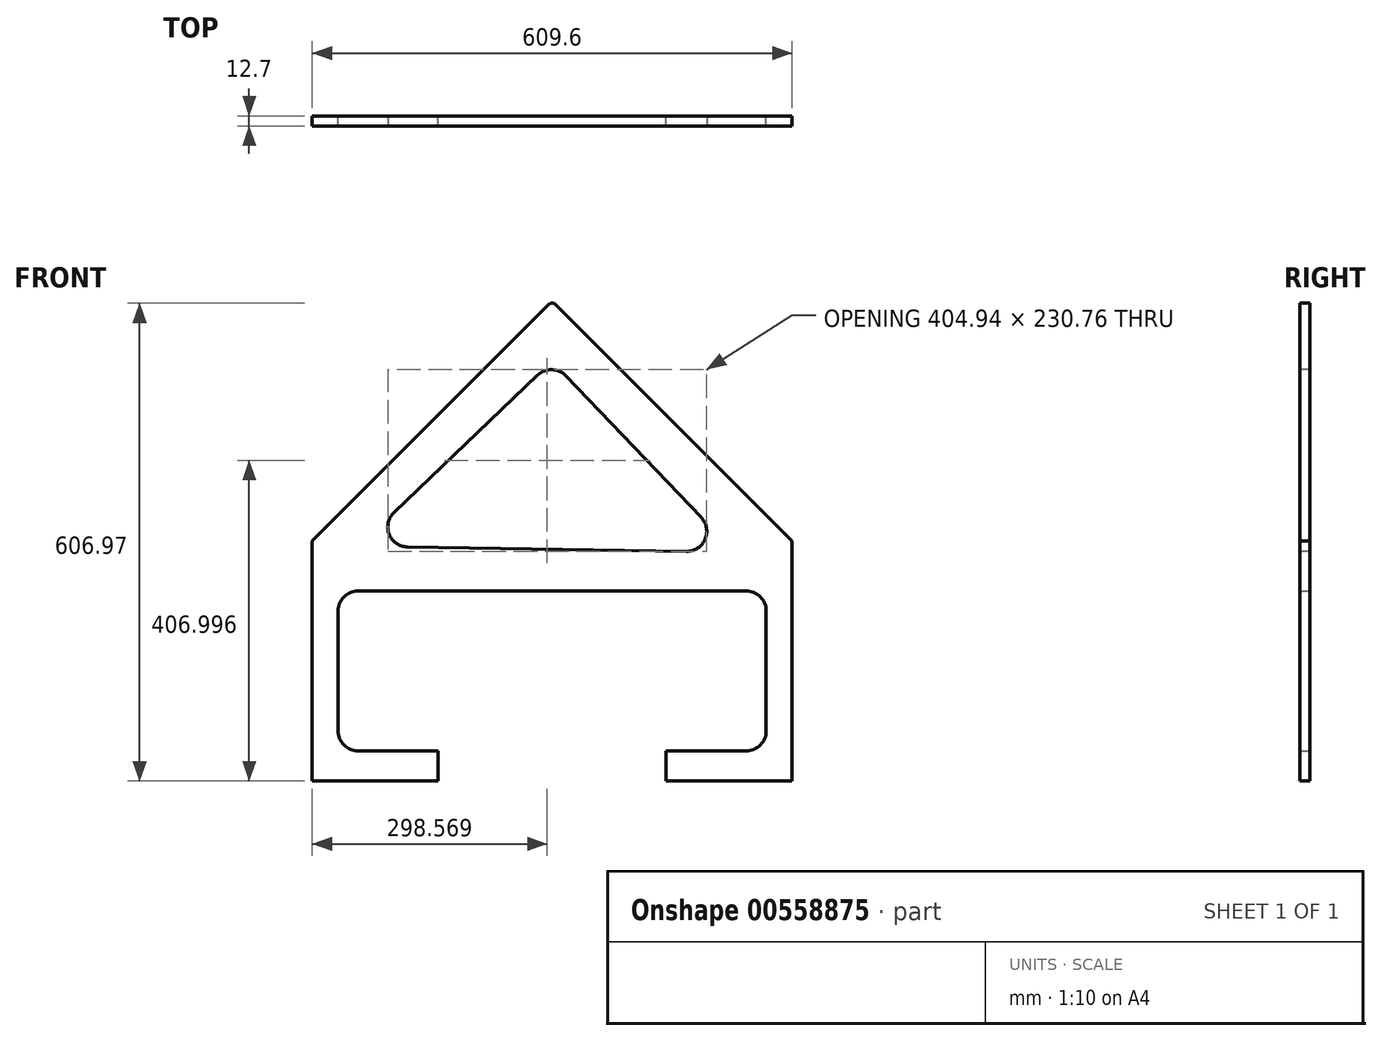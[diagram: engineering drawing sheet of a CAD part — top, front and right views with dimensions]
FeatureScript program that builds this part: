
annotation { "Feature Type Name" : "Feature", "Feature Type Description" : "" }
export const myFeature = defineFeature(function(context is Context, id is Id, definition is map)
    precondition{}
    {
        {
            var Q0;
            Q0=qCreatedBy(makeId("Front.planeOp"),FACE);
            var sketch = newSketch(context, id + "F0", { "sketchPlane" : qUnion([Q0])});
            skLineSegment(sketch, "E0", {"start": v(-304.8, 0) * mm, "end": v(-304.8, 304.8) * mm});
            skLineSegment(sketch, "E1", {"start": v(-304.8, 304.8) * mm, "end": v(0, 609.6) * mm});
            skLineSegment(sketch, "E2", {"start": v(-304.8, 0) * mm, "end": v(-144.82, 0) * mm});
            skLineSegment(sketch, "E3", {"start": v(-144.82, 0) * mm, "end": v(-144.82, 38.1) * mm});
            skLineSegment(sketch, "E4", {"start": v(-144.82, 38.1) * mm, "end": v(-271.82, 38.1) * mm});
            skLineSegment(sketch, "E5", {"start": v(-271.82, 38.1) * mm, "end": v(-271.82, 241.3) * mm});
            skLineSegment(sketch, "E6", {"start": v(-271.82, 241.3) * mm, "end": v(0, 241.3) * mm});
            skLineSegment(sketch, "E7", {"start": v(0, 287.8) * mm, "end": v(-247.66, 287.8) * mm, "construction": true});
            skLineSegment(sketch, "E8", {"start": v(-247.66, 287.8) * mm, "end": v(0, 535.45) * mm, "construction": true});
            skLineSegment(sketch, "E9.MirrorCS", {"start": v(304.8, 304.8) * mm, "end": v(0, 609.6) * mm});
            skLineSegment(sketch, "E10.MirrorCS", {"start": v(247.66, 287.8) * mm, "end": v(0, 535.45) * mm, "construction": true});
            skLineSegment(sketch, "E11.MirrorCS", {"start": v(0, 287.8) * mm, "end": v(247.66, 287.8) * mm, "construction": true});
            skLineSegment(sketch, "E12.MirrorCS", {"start": v(271.82, 241.3) * mm, "end": v(0, 241.3) * mm});
            skLineSegment(sketch, "E13.MirrorCS", {"start": v(304.8, 0) * mm, "end": v(304.8, 304.8) * mm});
            skLineSegment(sketch, "E14.MirrorCS", {"start": v(271.82, 38.1) * mm, "end": v(271.82, 241.3) * mm});
            skLineSegment(sketch, "E15.MirrorCS", {"start": v(144.82, 38.1) * mm, "end": v(271.82, 38.1) * mm});
            skLineSegment(sketch, "E16.MirrorCS", {"start": v(304.8, 0) * mm, "end": v(144.82, 0) * mm});
            skLineSegment(sketch, "E17.MirrorCS", {"start": v(144.82, 0) * mm, "end": v(144.82, 38.1) * mm});
            skSolve(sketch);
        }
        {
            var Q0;
            Q0=makeQuery(id+"F0.imprint","IMPRINT",FACE,{"disambiguationData":[TD([[makeQuery(id+"F0.imprint","IMPRINT",EDGE,{"derivedFrom":sQuery(id+"F0.wireOp",EDGE,"E0")}),-1.0]])]});
            extrude(context, id + "F1", {"entities" : qUnion([Q0]), "depth" : 12.7 * mm, "offsetDistance" : 25.4 * mm});
        }
        {
            var Q0;
            Q0=qCreatedBy(makeId("Front.planeOp"),FACE);
            var sketch = newSketch(context, id + "F2", { "sketchPlane" : qUnion([Q0])});
            skLineSegment(sketch, "E18", {"start": v(-245.72, 298.27) * mm, "end": v(0, 532.9) * mm});
            skLineSegment(sketch, "E19", {"start": v(0, 532.9) * mm, "end": v(231.31, 290.65) * mm});
            skLineSegment(sketch, "E20", {"start": v(231.31, 290.65) * mm, "end": v(-245.72, 298.27) * mm});
            skSolve(sketch);
        }
        {
            var Q0;
            Q0 = qSketchRegion(id + "F2", true);
            extrude(context, id + "F3", {"entities" : qUnion([Q0]), "operationType" : NewBodyOperationType.REMOVE, "endBound" : BoundingType.THROUGH_ALL, "depth" : 25.4 * mm, "offsetDistance" : 25.4 * mm});
        }
        {
            var Q0;
            Q0=makeQuery(id+"F1.opExtrude","SWEPT_EDGE",EDGE,{"disambiguationData":[OSD([sQuery(id+"F0.wireOp",EDGE,"E1"),sQuery(id+"F0.wireOp",EDGE,"E9.MirrorCS")])]});
            fillet(context, id + "F4", {"entities" : qUnion([Q0]), "radius" : 6.35 * mm, "tangentPropagation" : true, "allowEdgeOverflow" : false});
        }
        {
            var Q0;
            Q0=makeQuery(id+"F1.opExtrude","SWEPT_EDGE",EDGE,{"disambiguationData":[OSD([sQuery(id+"F0.wireOp",EDGE,"E4"),sQuery(id+"F0.wireOp",EDGE,"E5")])]});
            var Q1;
            Q1=makeQuery(id+"F1.opExtrude","SWEPT_EDGE",EDGE,{"disambiguationData":[OSD([sQuery(id+"F0.wireOp",EDGE,"E5"),sQuery(id+"F0.wireOp",EDGE,"E6")])]});
            var Q2;
            Q2=makeQuery(id+"F1.opExtrude","SWEPT_EDGE",EDGE,{"disambiguationData":[OSD([sQuery(id+"F0.wireOp",EDGE,"E12.MirrorCS"),sQuery(id+"F0.wireOp",EDGE,"E14.MirrorCS")])]});
            var Q3;
            Q3=makeQuery(id+"F1.opExtrude","SWEPT_EDGE",EDGE,{"disambiguationData":[OSD([sQuery(id+"F0.wireOp",EDGE,"E14.MirrorCS"),sQuery(id+"F0.wireOp",EDGE,"E15.MirrorCS")])]});
            var Q4;
            Q4=makeQuery(id+"F3.boolean.opBoolean","COPY",EDGE,{"derivedFrom":makeQuery(id+"F3.opExtrude","SWEPT_EDGE",EDGE,{"disambiguationData":[OSD([sQuery(id+"F2.wireOp",EDGE,"E18"),sQuery(id+"F2.wireOp",EDGE,"E20")])]})});
            var Q5;
            Q5=makeQuery(id+"F3.boolean.opBoolean","COPY",EDGE,{"derivedFrom":makeQuery(id+"F3.opExtrude","SWEPT_EDGE",EDGE,{"disambiguationData":[OSD([sQuery(id+"F2.wireOp",EDGE,"E19"),sQuery(id+"F2.wireOp",EDGE,"E20")])]})});
            var Q6;
            Q6=makeQuery(id+"F3.boolean.opBoolean","COPY",EDGE,{"derivedFrom":makeQuery(id+"F3.opExtrude","SWEPT_EDGE",EDGE,{"disambiguationData":[OSD([sQuery(id+"F2.wireOp",EDGE,"E18"),sQuery(id+"F2.wireOp",EDGE,"E19")])]})});
            fillet(context, id + "F5", {"entities" : qUnion([Q0, Q1, Q2, Q3, Q4, Q5, Q6]), "radius" : 25.4 * mm, "tangentPropagation" : true, "allowEdgeOverflow" : false});
        }
    });
